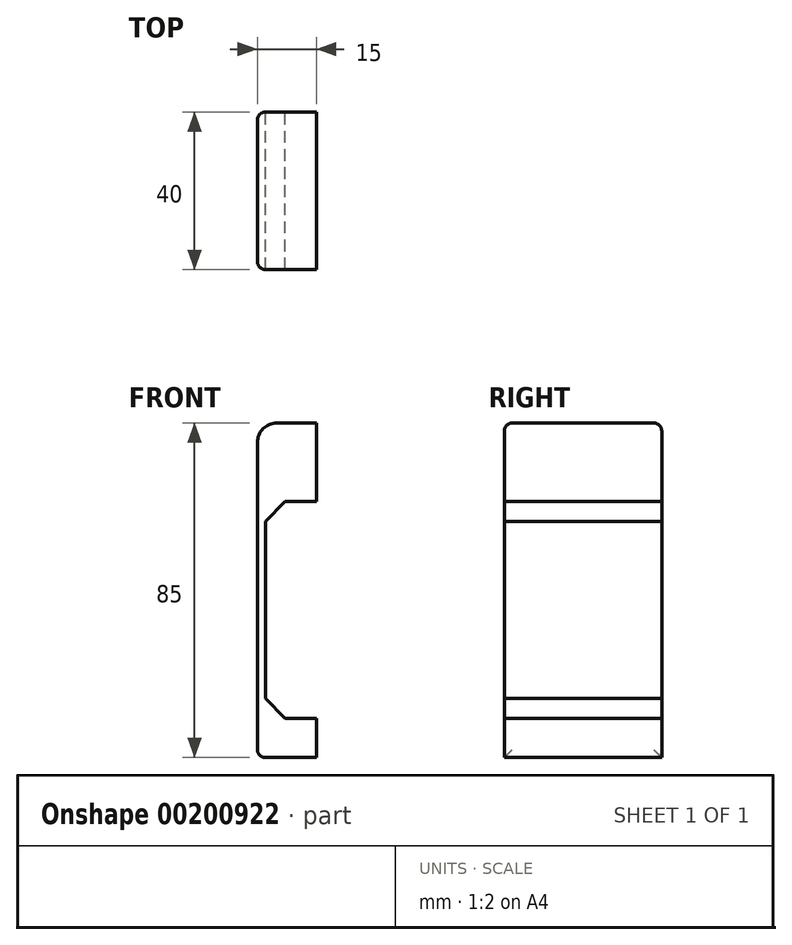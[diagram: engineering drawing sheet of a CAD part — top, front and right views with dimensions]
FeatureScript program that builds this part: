
annotation { "Feature Type Name" : "Feature", "Feature Type Description" : "" }
export const myFeature = defineFeature(function(context is Context, id is Id, definition is map)
    precondition{}
    {
        {
            var Q0;
            Q0=qCreatedBy(makeId("Front.planeOp"),FACE);
            var sketch = newSketch(context, id + "F0", { "sketchPlane" : qUnion([Q0])});
            skLineSegment(sketch, "E0", {"start": v(0, 56.24) * mm, "end": v(-15, 56.24) * mm});
            skLineSegment(sketch, "E1", {"start": v(-15, 56.24) * mm, "end": v(-15, 36.24) * mm});
            skLineSegment(sketch, "E2", {"start": v(-15, 36.24) * mm, "end": v(0, 36.24) * mm});
            skLineSegment(sketch, "E3", {"start": v(0, 36.24) * mm, "end": v(0, 56.24) * mm});
            skLineSegment(sketch, "E4", {"start": v(-15, 36.24) * mm, "end": v(-15, -28.76) * mm});
            skLineSegment(sketch, "E5", {"start": v(-15, -28.76) * mm, "end": v(0, -28.76) * mm});
            skLineSegment(sketch, "E6", {"start": v(0, -28.76) * mm, "end": v(0, -18.76) * mm});
            skLineSegment(sketch, "E7", {"start": v(0, -18.76) * mm, "end": v(-13, -18.76) * mm});
            skLineSegment(sketch, "E8", {"start": v(-13, -18.76) * mm, "end": v(-13, 36.24) * mm});
            skSolve(sketch);
        }
        {
            var Q0;
            {var subQ0=sQuery(id+"F0.wireOp",EDGE,"E4");Q0=makeQuery(id+"F0.imprint","IMPRINT",FACE,{"disambiguationData":[TD([[makeQuery(id+"F0.imprint","IMPRINT",EDGE,{"derivedFrom":subQ0}),1.0]])]});}
            var Q1;
            Q1=makeQuery(id+"F0.imprint","IMPRINT",FACE,{"disambiguationData":[TD([[makeQuery(id+"F0.imprint","IMPRINT",EDGE,{"derivedFrom":sQuery(id+"F0.wireOp",EDGE,"E0")}),1.0]])]});
            extrude(context, id + "F1", {"entities" : qUnion([Q0, Q1]), "depth" : 40 * mm, "offsetDistance" : 25 * mm});
        }
        {
            var Q0;
            Q0=makeQuery(id+"F1.opExtrude","SWEPT_EDGE",EDGE,{"disambiguationData":[OSD([sQuery(id+"F0.wireOp",EDGE,"E7"),sQuery(id+"F0.wireOp",EDGE,"E8")])]});
            var Q1;
            Q1=makeQuery(id+"F1.opExtrude","SWEPT_EDGE",EDGE,{"disambiguationData":[OSD([sQuery(id+"F0.wireOp",EDGE,"E2"),sQuery(id+"F0.wireOp",EDGE,"E8")])]});
            chamfer(context, id + "F2", {"entities" : qUnion([Q0, Q1]), "width" : 5 * mm, "tangentPropagation" : true});
        }
        {
            var Q0;
            Q0=makeQuery(id+"F1.opExtrude","SWEPT_EDGE",EDGE,{"disambiguationData":[OSD([sQuery(id+"F0.wireOp",EDGE,"E0"),sQuery(id+"F0.wireOp",EDGE,"E1")])]});
            fillet(context, id + "F3", {"entities" : qUnion([Q0]), "radius" : 5 * mm, "tangentPropagation" : true, "allowEdgeOverflow" : false});
        }
        {
            var Q0;
            Q0=makeQuery(id+"F1.opExtrude","SWEPT_FACE",FACE,{"disambiguationData":[OSD([sQuery(id+"F0.wireOp",EDGE,"E1"),sQuery(id+"F0.wireOp",EDGE,"E4")])]});
            fillet(context, id + "F4", {"entities" : qUnion([Q0]), "radius" : 2 * mm, "tangentPropagation" : true, "allowEdgeOverflow" : false});
        }
    });
